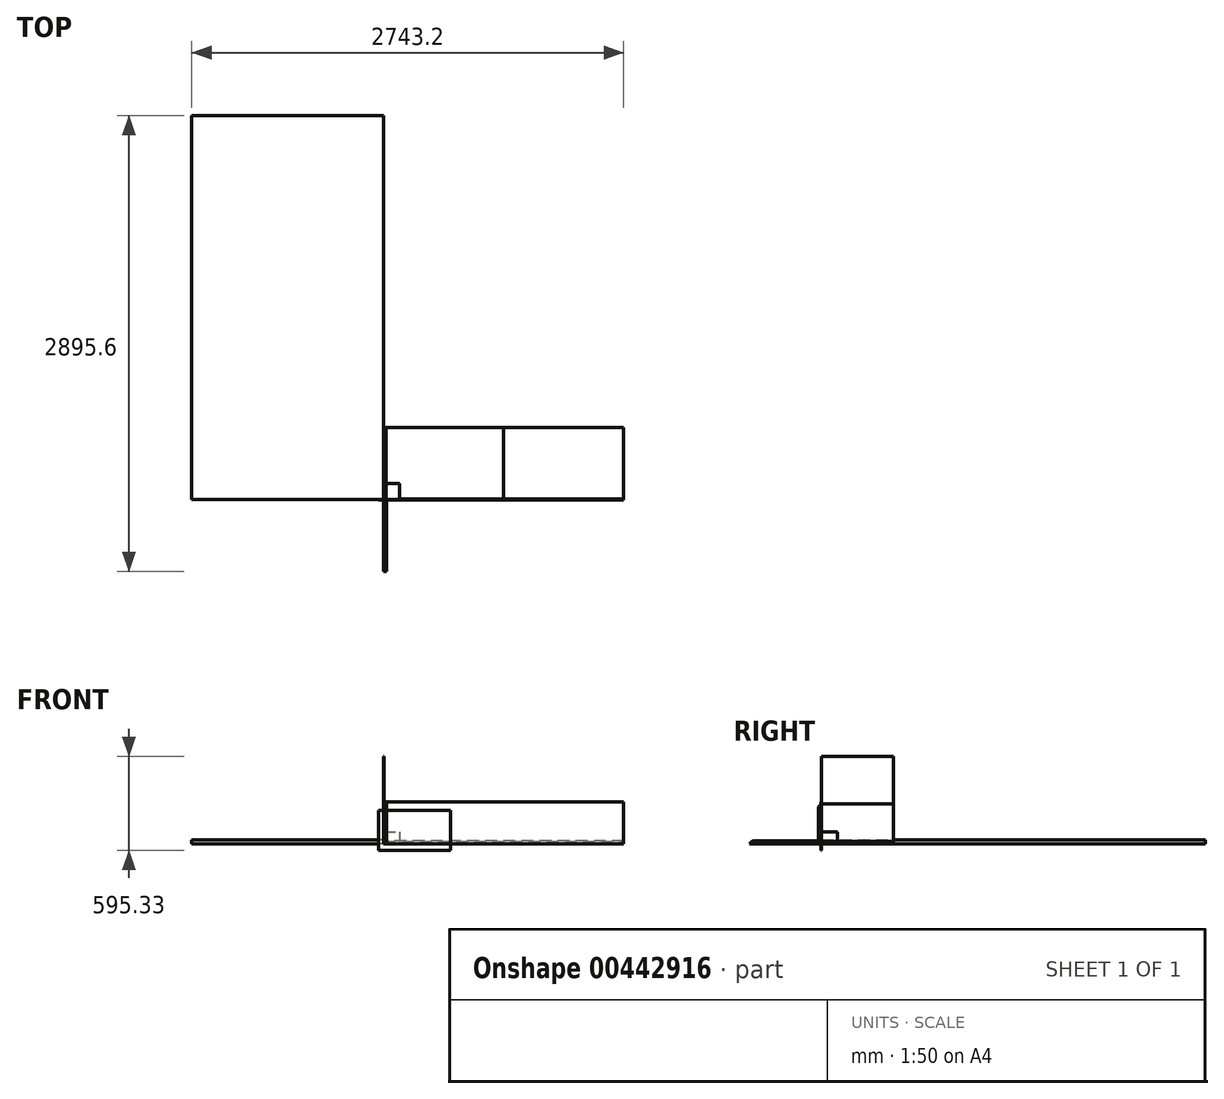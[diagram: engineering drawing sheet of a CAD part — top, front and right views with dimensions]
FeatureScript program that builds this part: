
annotation { "Feature Type Name" : "Feature", "Feature Type Description" : "" }
export const myFeature = defineFeature(function(context is Context, id is Id, definition is map)
    precondition{}
    {
        {
            var Q0;
            Q0=qCreatedBy(makeId("Top.planeOp"),FACE);
            var sketch = newSketch(context, id + "F0", { "sketchPlane" : qUnion([Q0])});
            skLineSegment(sketch, "E0.bottom", {"start": v(0, 0) * mm, "end": v(1524, 0) * mm});
            skLineSegment(sketch, "E0.top", {"start": v(0, 457.2) * mm, "end": v(1524, 457.2) * mm});
            skLineSegment(sketch, "E0.left", {"start": v(0, 0) * mm, "end": v(0, 457.2) * mm});
            skLineSegment(sketch, "E0.right", {"start": v(1524, 0) * mm, "end": v(1524, 457.2) * mm});
            skSolve(sketch);
        }
        {
            var Q0;
            Q0=makeQuery(id+"F0.imprint","IMPRINT",FACE,{"disambiguationData":[TD([[makeQuery(id+"F0.imprint","IMPRINT",EDGE,{"derivedFrom":sQuery(id+"F0.wireOp",EDGE,"E0.bottom")}),1.0]])]});
            extrude(context, id + "F1", {"entities" : qUnion([Q0]), "depth" : 15.88 * mm});
        }
        {
            var Q0;
            Q0=qCreatedBy(makeId("Right.planeOp"),FACE);
            var sketch = newSketch(context, id + "F2", { "sketchPlane" : qUnion([Q0])});
            skLineSegment(sketch, "E1.bottom", {"start": v(0, 0) * mm, "end": v(457.2, 0) * mm});
            skLineSegment(sketch, "E1.top", {"start": v(0, 254) * mm, "end": v(457.2, 254) * mm});
            skLineSegment(sketch, "E1.left", {"start": v(0, 0) * mm, "end": v(0, 254) * mm});
            skLineSegment(sketch, "E1.right", {"start": v(457.2, 0) * mm, "end": v(457.2, 254) * mm});
            skSolve(sketch);
        }
        {
            var Q0;
            Q0=makeQuery(id+"F2.imprint","IMPRINT",FACE,{"disambiguationData":[TD([[makeQuery(id+"F2.imprint","IMPRINT",EDGE,{"derivedFrom":sQuery(id+"F2.wireOp",EDGE,"E1.bottom")}),1.0]])]});
            extrude(context, id + "F3", {"entities" : qUnion([Q0]), "depth" : 15.88 * mm});
        }
        {
            var Q0;
            Q0=qCreatedBy(makeId("Top.planeOp"),FACE);
            var sketch = newSketch(context, id + "F4", { "sketchPlane" : qUnion([Q0])});
            skLineSegment(sketch, "E2.bottom", {"start": v(0, 0) * mm, "end": v(101.6, 0) * mm});
            skLineSegment(sketch, "E2.top", {"start": v(0, 101.6) * mm, "end": v(101.6, 101.6) * mm});
            skLineSegment(sketch, "E2.left", {"start": v(0, 0) * mm, "end": v(0, 101.6) * mm});
            skLineSegment(sketch, "E2.right", {"start": v(101.6, 0) * mm, "end": v(101.6, 101.6) * mm});
            skSolve(sketch);
        }
        {
            var Q0;
            Q0=makeQuery(id+"F4.imprint","IMPRINT",FACE,{"disambiguationData":[TD([[makeQuery(id+"F4.imprint","IMPRINT",EDGE,{"derivedFrom":sQuery(id+"F4.wireOp",EDGE,"E2.bottom")}),1.0]])]});
            extrude(context, id + "F5", {"entities" : qUnion([Q0]), "depth" : 76.2 * mm});
        }
        {
            var Q0;
            Q0=qCreatedBy(makeId("Right.planeOp"),FACE);
            var sketch = newSketch(context, id + "F6", { "sketchPlane" : qUnion([Q0])});
            skLineSegment(sketch, "E3", {"start": v(0, 0) * mm, "end": v(0, 19.05) * mm});
            skLineSegment(sketch, "E4", {"start": v(0, 19.05) * mm, "end": v(3.17, 19.05) * mm});
            skLineSegment(sketch, "E5", {"start": v(3.17, 19.05) * mm, "end": v(3.18, 3.17) * mm});
            skLineSegment(sketch, "E6", {"start": v(3.18, 3.17) * mm, "end": v(19.05, 3.18) * mm});
            skLineSegment(sketch, "E7", {"start": v(19.05, 3.18) * mm, "end": v(19.05, 0) * mm});
            skLineSegment(sketch, "E8", {"start": v(19.05, 0) * mm, "end": v(0, 0) * mm});
            skSolve(sketch);
        }
        {
            var Q0;
            Q0=makeQuery(id+"F6.imprint","IMPRINT",FACE,{"disambiguationData":[TD([[makeQuery(id+"F6.imprint","IMPRINT",EDGE,{"derivedFrom":sQuery(id+"F6.wireOp",EDGE,"E3")}),-1.0]])]});
            extrude(context, id + "F7", {"entities" : qUnion([Q0]), "depth" : 1524 * mm});
        }
        {
            var Q0;
            Q0=qCreatedBy(makeId("Front.planeOp"),FACE);
            var sketch = newSketch(context, id + "F8", { "sketchPlane" : qUnion([Q0])});
            skLineSegment(sketch, "E9.bottom", {"start": v(0, 0) * mm, "end": v(19.05, 0) * mm});
            skLineSegment(sketch, "E9.top", {"start": v(0, 19.05) * mm, "end": v(19.05, 19.05) * mm});
            skLineSegment(sketch, "E9.left", {"start": v(0, 0) * mm, "end": v(0, 19.05) * mm});
            skLineSegment(sketch, "E9.right", {"start": v(19.05, 0) * mm, "end": v(19.05, 19.05) * mm});
            skSolve(sketch);
        }
        {
            var Q0;
            Q0=makeQuery(id+"F8.imprint","IMPRINT",FACE,{"disambiguationData":[TD([[makeQuery(id+"F8.imprint","IMPRINT",EDGE,{"derivedFrom":sQuery(id+"F8.wireOp",EDGE,"E9.bottom")}),1.0]])]});
            extrude(context, id + "F9", {"entities" : qUnion([Q0]), "depth" : 457.2 * mm});
        }
        {
            var Q0;
            Q0=makeQuery(id+"F9.opExtrude","CAP_EDGE",EDGE,{"disambiguationData":[OSD([sQuery(id+"F8.wireOp",EDGE,"E9.top")])],"isStart":false});
            var Q1;
            Q1=makeQuery(id+"F9.opExtrude","CAP_EDGE",EDGE,{"disambiguationData":[OSD([sQuery(id+"F8.wireOp",EDGE,"E9.top")])],"isStart":true});
            chamfer(context, id + "F10", {"entities" : qUnion([Q0, Q1]), "width" : 19.05 * mm, "tangentPropagation" : true});
        }
        {
            var Q0;
            Q0=qCreatedBy(makeId("Top.planeOp"),FACE);
            var sketch = newSketch(context, id + "F11", { "sketchPlane" : qUnion([Q0])});
            skLineSegment(sketch, "E10.bottom", {"start": v(0, 0) * mm, "end": v(19.05, 0) * mm});
            skLineSegment(sketch, "E10.top", {"start": v(0, -19.05) * mm, "end": v(19.05, -19.05) * mm});
            skLineSegment(sketch, "E10.left", {"start": v(0, 0) * mm, "end": v(0, -19.05) * mm});
            skLineSegment(sketch, "E10.right", {"start": v(19.05, 0) * mm, "end": v(19.05, -19.05) * mm});
            skSolve(sketch);
        }
        {
            var Q0;
            Q0=makeQuery(id+"F11.imprint","IMPRINT",FACE,{"disambiguationData":[TD([[makeQuery(id+"F11.imprint","IMPRINT",EDGE,{"derivedFrom":sQuery(id+"F11.wireOp",EDGE,"E10.bottom")}),-1.0]])]});
            extrude(context, id + "F12", {"entities" : qUnion([Q0]), "depth" : 254 * mm});
        }
        {
            var Q0;
            Q0=makeQuery(id+"F12.opExtrude","CAP_EDGE",EDGE,{"disambiguationData":[OSD([sQuery(id+"F11.wireOp",EDGE,"E10.top")])],"isStart":false});
            var Q1;
            Q1=makeQuery(id+"F12.opExtrude","CAP_EDGE",EDGE,{"disambiguationData":[OSD([sQuery(id+"F11.wireOp",EDGE,"E10.top")])],"isStart":true});
            chamfer(context, id + "F13", {"entities" : qUnion([Q0, Q1]), "width" : 19.05 * mm, "tangentPropagation" : true});
        }
        {
            var Q0;
            Q0=qCreatedBy(makeId("Front.planeOp"),FACE);
            var sketch = newSketch(context, id + "F14", { "sketchPlane" : qUnion([Q0])});
            skLineSegment(sketch, "E11.bottom", {"start": v(-34.2, -39.71) * mm, "end": v(423, -39.71) * mm});
            skLineSegment(sketch, "E11.top", {"start": v(-34.2, 214.29) * mm, "end": v(423, 214.29) * mm});
            skLineSegment(sketch, "E11.left", {"start": v(-34.2, -39.71) * mm, "end": v(-34.2, 214.29) * mm});
            skLineSegment(sketch, "E11.right", {"start": v(423, -39.71) * mm, "end": v(423, 214.29) * mm});
            skSolve(sketch);
        }
        {
            var Q0;
            Q0=makeQuery(id+"F14.imprint","IMPRINT",FACE,{"disambiguationData":[TD([[makeQuery(id+"F14.imprint","IMPRINT",EDGE,{"derivedFrom":sQuery(id+"F14.wireOp",EDGE,"E11.bottom")}),1.0]])]});
            extrude(context, id + "F15", {"entities" : qUnion([Q0]), "depth" : 3.17 * mm});
        }
        {
            var Q0;
            Q0=qCreatedBy(makeId("Right.planeOp"),FACE);
            var sketch = newSketch(context, id + "F16", { "sketchPlane" : qUnion([Q0])});
            skLineSegment(sketch, "E12.bottom", {"start": v(0, 0) * mm, "end": v(457.2, 0) * mm});
            skLineSegment(sketch, "E12.top", {"start": v(0, 555.62) * mm, "end": v(457.2, 555.62) * mm});
            skLineSegment(sketch, "E12.left", {"start": v(0, 0) * mm, "end": v(0, 555.62) * mm});
            skLineSegment(sketch, "E12.right", {"start": v(457.2, 0) * mm, "end": v(457.2, 555.62) * mm});
            skSolve(sketch);
        }
        {
            var Q0;
            Q0=makeQuery(id+"F16.imprint","IMPRINT",FACE,{"disambiguationData":[TD([[makeQuery(id+"F16.imprint","IMPRINT",EDGE,{"derivedFrom":sQuery(id+"F16.wireOp",EDGE,"E12.bottom")}),1.0]])]});
            extrude(context, id + "F17", {"entities" : qUnion([Q0]), "depth" : 3.17 * mm});
        }
        {
            var Q0;
            Q0=qCreatedBy(makeId("Front.planeOp"),FACE);
            var sketch = newSketch(context, id + "F18", { "sketchPlane" : qUnion([Q0])});
            skLineSegment(sketch, "E13.bottom", {"start": v(0, 0) * mm, "end": v(1524, 0) * mm});
            skLineSegment(sketch, "E13.top", {"start": v(0, 266.7) * mm, "end": v(1524, 266.7) * mm});
            skLineSegment(sketch, "E13.left", {"start": v(0, 0) * mm, "end": v(0, 266.7) * mm});
            skLineSegment(sketch, "E13.right", {"start": v(1524, 0) * mm, "end": v(1524, 266.7) * mm});
            skSolve(sketch);
        }
        {
            var Q0;
            Q0=makeQuery(id+"F18.imprint","IMPRINT",FACE,{"disambiguationData":[TD([[makeQuery(id+"F18.imprint","IMPRINT",EDGE,{"derivedFrom":sQuery(id+"F18.wireOp",EDGE,"E13.bottom")}),1.0]])]});
            extrude(context, id + "F19", {"entities" : qUnion([Q0]), "depth" : 3.17 * mm});
        }
        {
            var Q0;
            Q0=qCreatedBy(makeId("Top.planeOp"),FACE);
            var sketch = newSketch(context, id + "F20", { "sketchPlane" : qUnion([Q0])});
            skLineSegment(sketch, "E14.bottom", {"start": v(0, 0) * mm, "end": v(-1219.2, 0) * mm});
            skLineSegment(sketch, "E14.top", {"start": v(0, 2438.4) * mm, "end": v(-1219.2, 2438.4) * mm});
            skLineSegment(sketch, "E14.left", {"start": v(0, 0) * mm, "end": v(0, 2438.4) * mm});
            skLineSegment(sketch, "E14.right", {"start": v(-1219.2, 0) * mm, "end": v(-1219.2, 2438.4) * mm});
            skSolve(sketch);
        }
        {
            var Q0;
            Q0=qCreatedBy(makeId("Top.planeOp"),FACE);
            var sketch = newSketch(context, id + "F21", { "sketchPlane" : qUnion([Q0])});
            skLineSegment(sketch, "E15.bottom", {"start": v(0, 0) * mm, "end": v(762, 0) * mm});
            skLineSegment(sketch, "E15.top", {"start": v(0, 457.2) * mm, "end": v(762, 457.2) * mm});
            skLineSegment(sketch, "E15.left", {"start": v(0, 0) * mm, "end": v(0, 457.2) * mm});
            skLineSegment(sketch, "E15.right", {"start": v(762, 0) * mm, "end": v(762, 457.2) * mm});
            skSolve(sketch);
        }
        {
            var Q0;
            Q0=makeQuery(id+"F21.imprint","IMPRINT",FACE,{"disambiguationData":[TD([[makeQuery(id+"F21.imprint","IMPRINT",EDGE,{"derivedFrom":sQuery(id+"F21.wireOp",EDGE,"E15.bottom")}),1.0]])]});
            extrude(context, id + "F22", {"entities" : qUnion([Q0]), "depth" : 15.88 * mm});
        }
        {
            var Q0;
            Q0 = qSketchRegion(id + "F20", true);
            extrude(context, id + "F23", {"entities" : qUnion([Q0]), "depth" : 25.4 * mm});
        }
    });
